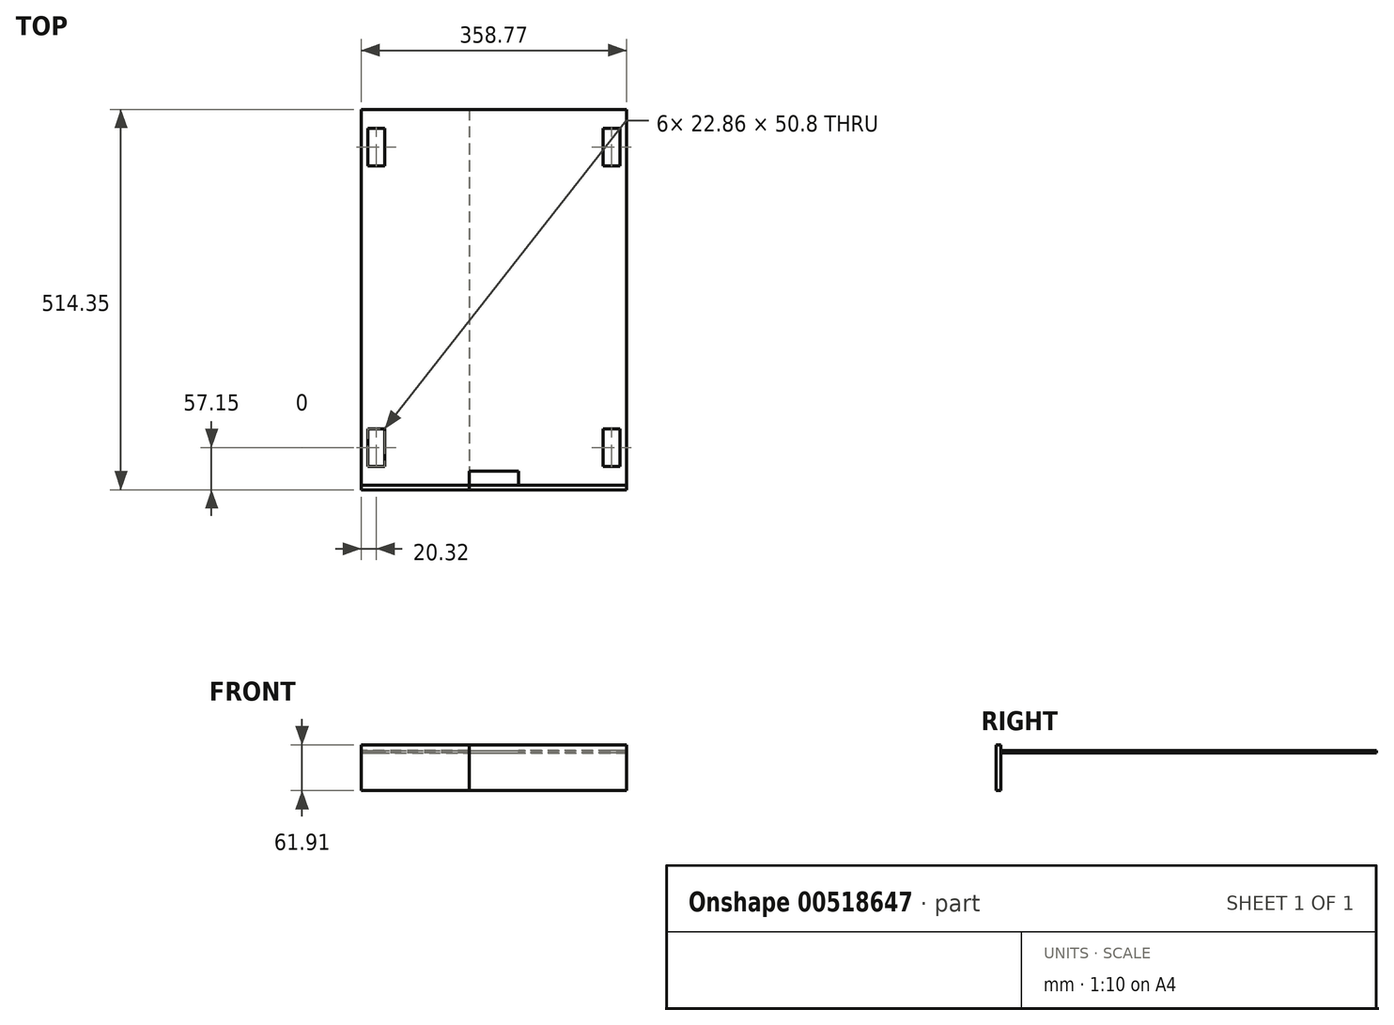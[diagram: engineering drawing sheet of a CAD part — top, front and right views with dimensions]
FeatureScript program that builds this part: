
annotation { "Feature Type Name" : "Feature", "Feature Type Description" : "" }
export const myFeature = defineFeature(function(context is Context, id is Id, definition is map)
    precondition{}
    {
        {
            var Q0;
            Q0=qCreatedBy(makeId("Front.planeOp"),FACE);
            var sketch = newSketch(context, id + "F0", { "sketchPlane" : qUnion([Q0])});
            skLineSegment(sketch, "E0.bottom", {"start": v(-29.05, 10.66) * mm, "end": v(329.72, 10.66) * mm});
            skLineSegment(sketch, "E0.top", {"start": v(-29.05, -51.25) * mm, "end": v(329.72, -51.25) * mm});
            skLineSegment(sketch, "E0.left", {"start": v(-29.05, 10.66) * mm, "end": v(-29.05, -51.25) * mm});
            skLineSegment(sketch, "E0.right", {"start": v(329.72, 10.66) * mm, "end": v(329.72, -51.25) * mm});
            skLineSegment(sketch, "E1", {"start": v(117, 10.66) * mm, "end": v(117, -51.25) * mm});
            skSolve(sketch);
        }
        {
            var Q0;
            Q0=makeQuery(id+"F0.imprint","IMPRINT",FACE,{"disambiguationData":[TD([[makeQuery(id+"F0.imprint","IMPRINT",EDGE,{"derivedFrom":sQuery(id+"F0.wireOp",EDGE,"E0.bottom")}),-1.0]])]});
            extrude(context, id + "F1", {"entities" : qUnion([Q0]), "depth" : 6.35 * mm});
        }
        {
            var Q0;
            {var subQ0=sQuery(id+"F0.wireOp",EDGE,"E0.left");Q0=makeQuery(id+"F0.imprint","IMPRINT",FACE,{"disambiguationData":[TD([[makeQuery(id+"F0.imprint","IMPRINT",EDGE,{"derivedFrom":subQ0}),1.0]])]});}
            extrude(context, id + "F2", {"entities" : qUnion([Q0]), "depth" : 6.35 * mm});
        }
        {
            var Q0;
            Q0=qCreatedBy(makeId("Top.planeOp"),FACE);
            var sketch = newSketch(context, id + "F3", { "sketchPlane" : qUnion([Q0])});
            skPoint(sketch, "E2.0", {"position": v(-29.05, 0) * mm});
            skPoint(sketch, "E2.1", {"position": v(117, 0) * mm});
            skLineSegment(sketch, "E3", {"start": v(-29.05, 0) * mm, "end": v(-29.05, 508) * mm});
            skLineSegment(sketch, "E4", {"start": v(-29.05, 508) * mm, "end": v(117, 508) * mm});
            skLineSegment(sketch, "E5", {"start": v(117, 508) * mm, "end": v(117, 0) * mm});
            skLineSegment(sketch, "E6", {"start": v(117, 0) * mm, "end": v(-29.05, 0) * mm});
            skLineSegment(sketch, "E7.bottom", {"start": v(-20.16, 482.6) * mm, "end": v(2.7, 482.6) * mm});
            skLineSegment(sketch, "E7.top", {"start": v(-20.16, 431.8) * mm, "end": v(2.7, 431.8) * mm});
            skLineSegment(sketch, "E7.left", {"start": v(-20.16, 482.6) * mm, "end": v(-20.16, 431.8) * mm});
            skLineSegment(sketch, "E7.right", {"start": v(2.7, 482.6) * mm, "end": v(2.7, 431.8) * mm});
            skPoint(sketch, "E8", {"position": v(-20.16, 457.2) * mm});
            skLineSegment(sketch, "E9", {"start": v(-29.05, 254) * mm, "end": v(117, 254) * mm, "construction": true});
            skLineSegment(sketch, "E10.MirrorCS", {"start": v(-20.16, 76.2) * mm, "end": v(2.7, 76.2) * mm});
            skLineSegment(sketch, "E11.MirrorCS", {"start": v(-20.16, 25.4) * mm, "end": v(-20.16, 76.2) * mm});
            skLineSegment(sketch, "E12.MirrorCS", {"start": v(2.7, 25.4) * mm, "end": v(2.7, 76.2) * mm});
            skLineSegment(sketch, "E13.MirrorCS", {"start": v(-20.16, 25.4) * mm, "end": v(2.7, 25.4) * mm});
            skSolve(sketch);
        }
        {
            var Q0;
            Q0=makeQuery(id+"F3.imprint","IMPRINT",FACE,{"disambiguationData":[TD([[makeQuery(id+"F3.imprint","IMPRINT",EDGE,{"derivedFrom":sQuery(id+"F3.wireOp",EDGE,"E3")}),-1.0]])]});
            extrude(context, id + "F4", {"entities" : qUnion([Q0]), "depth" : 1.59 * mm});
        }
        {
            var Q0;
            Q0=qCreatedBy(makeId("Top.planeOp"),FACE);
            var sketch = newSketch(context, id + "F5", { "sketchPlane" : qUnion([Q0])});
            skLineSegment(sketch, "E14.0", {"start": v(-29.05, 0) * mm, "end": v(-29.05, 508) * mm});
            skLineSegment(sketch, "E15", {"start": v(-29.05, 508) * mm, "end": v(329.72, 508) * mm});
            skLineSegment(sketch, "E16", {"start": v(329.72, 508) * mm, "end": v(329.72, 0) * mm});
            skLineSegment(sketch, "E17", {"start": v(329.72, 0) * mm, "end": v(-29.05, 0) * mm});
            skLineSegment(sketch, "E18", {"start": v(-29.05, 254) * mm, "end": v(329.72, 254) * mm, "construction": true});
            skLineSegment(sketch, "E19", {"start": v(150.34, 508) * mm, "end": v(150.34, 0) * mm, "construction": true});
            skPoint(sketch, "E20", {"position": v(320.83, 457.2) * mm});
            skLineSegment(sketch, "E21.0", {"start": v(-20.16, 482.6) * mm, "end": v(2.7, 482.6) * mm});
            skLineSegment(sketch, "E21.1", {"start": v(-20.16, 482.6) * mm, "end": v(-20.16, 431.8) * mm});
            skLineSegment(sketch, "E21.2", {"start": v(2.7, 482.6) * mm, "end": v(2.7, 431.8) * mm});
            skLineSegment(sketch, "E21.3", {"start": v(-20.16, 431.8) * mm, "end": v(2.7, 431.8) * mm});
            skLineSegment(sketch, "E21.4", {"start": v(-20.16, 76.2) * mm, "end": v(2.7, 76.2) * mm});
            skLineSegment(sketch, "E21.5", {"start": v(2.7, 25.4) * mm, "end": v(2.7, 76.2) * mm});
            skLineSegment(sketch, "E21.6", {"start": v(-20.16, 25.4) * mm, "end": v(-20.16, 76.2) * mm});
            skLineSegment(sketch, "E21.7", {"start": v(-20.16, 25.4) * mm, "end": v(2.7, 25.4) * mm});
            skLineSegment(sketch, "E22.MirrorCS", {"start": v(320.83, 482.6) * mm, "end": v(297.97, 482.6) * mm});
            skLineSegment(sketch, "E23.MirrorCS", {"start": v(320.83, 482.6) * mm, "end": v(320.83, 431.8) * mm});
            skLineSegment(sketch, "E24.MirrorCS", {"start": v(297.97, 482.6) * mm, "end": v(297.97, 431.8) * mm});
            skLineSegment(sketch, "E25.MirrorCS", {"start": v(320.83, 431.8) * mm, "end": v(297.97, 431.8) * mm});
            skLineSegment(sketch, "E26.MirrorCS", {"start": v(320.83, 76.2) * mm, "end": v(297.97, 76.2) * mm});
            skLineSegment(sketch, "E27.MirrorCS", {"start": v(320.83, 25.4) * mm, "end": v(320.83, 76.2) * mm});
            skLineSegment(sketch, "E28.MirrorCS", {"start": v(297.97, 25.4) * mm, "end": v(297.97, 76.2) * mm});
            skLineSegment(sketch, "E29.MirrorCS", {"start": v(320.83, 25.4) * mm, "end": v(297.97, 25.4) * mm});
            skLineSegment(sketch, "E30", {"start": v(117, 0) * mm, "end": v(117, 19.05) * mm});
            skLineSegment(sketch, "E31", {"start": v(117, 19.05) * mm, "end": v(183.67, 19.05) * mm});
            skLineSegment(sketch, "E32", {"start": v(183.67, 19.05) * mm, "end": v(183.67, 0) * mm});
            skSolve(sketch);
        }
        {
            var Q0;
            Q0=makeQuery(id+"F5.imprint","IMPRINT",FACE,{"disambiguationData":[TD([[makeQuery(id+"F5.imprint","IMPRINT",EDGE,{"derivedFrom":sQuery(id+"F5.wireOp",EDGE,"E14.0")}),-1.0]])]});
            extrude(context, id + "F6", {"entities" : qUnion([Q0]), "depth" : 3.17 * mm});
        }
    });
